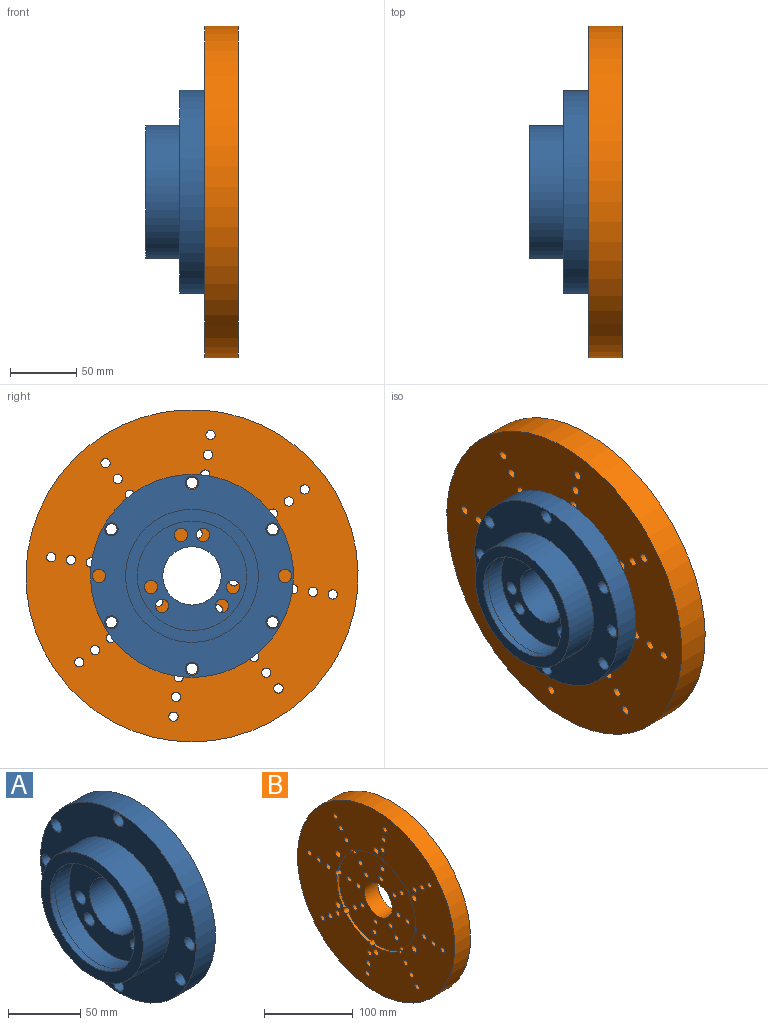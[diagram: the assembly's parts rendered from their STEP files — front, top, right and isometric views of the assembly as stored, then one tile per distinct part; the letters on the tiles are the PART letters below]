
ASSEMBLY  parts=2 mates=1
PART A: 59 faces, bbox 47.5x152.8x152.8 mm
  f0: cylinder r=8mm len=16mm, axis (1,0,0), area 508.6mm2, adj f7,f19,f31,f32
  f1: cylinder r=8mm len=16mm, axis (1,0,0), area 508.6mm2, adj f7,f19,f31,f32
  f2: cylinder r=8mm len=16mm, axis (1,0,0), area 508.6mm2, adj f7,f22,f29,f30
  f3: cylinder r=8mm len=15.96mm, axis (1,0,0), area 508.6mm2, adj f7,f22,f29,f30
  f4: cylinder r=8mm len=15.96mm, axis (1,0,0), area 508.6mm2, adj f7,f25,f27,f28
  f5: cylinder r=8mm len=16mm, axis (1,0,0), area 508.6mm2, adj f7,f25,f27,f28
  f6: cylinder r=22mm len=44mm, axis (-1,0,0), area 3870.4mm2, adj f7,f17
  f7: plane 125x125mm, normal (1,0,0), area 9095.5mm2, adj f0,f1,f2,f3,f4,f5,f6,f8
  f8: cylinder r=62.5mm len=125mm, axis (-1,0,0), area 1178.1mm2, adj f7,f9
  f9: plane 152.75x152.75mm, normal (1,0,0), area 5425.2mm2, adj f8,f10,f33,f34,f35,f36,f37,f38
  f10: cylinder r=76.38mm len=152.75mm, axis (-1,0,0), area 9069.7mm2, adj f9,f11
  f11: plane 152.75x152.75mm, normal (-1,0,0), area 9843.1mm2, adj f10,f12,f33,f34,f35,f36,f37,f38
  f12: cylinder r=50mm len=100mm, axis (-1,0,0), area 8042.5mm2, adj f11,f13
  f13: plane 100x100mm, normal (-1,0,0), area 2508.4mm2, adj f12,f14
  f14: cylinder r=41.25mm len=82.5mm, axis (-1,0,0), area 1295.9mm2, adj f13,f15
  f15: plane 84x84mm, normal (1,0,0), area 196.2mm2, adj f14,f16
  f16: cylinder r=42mm len=84mm, axis (-1,0,0), area 3826.5mm2, adj f15,f17
  f17: plane 84x84mm, normal (-1,0,0), area 3550mm2, adj f6,f16,f18,f20,f21,f23,f24,f26
  f18: cylinder r=5mm len=13mm, axis (1,0,0), area 408.4mm2, adj f17,f19
  f19: plane 32.54x17.09mm, normal (1,0,0), area 298.2mm2, adj f0,f1,f18,f20,f31,f32
  f20: cylinder r=5mm len=13mm, axis (1,0,0), area 408.4mm2, adj f17,f19
  f21: cylinder r=5mm len=13mm, axis (1,0,0), area 408.4mm2, adj f17,f22
  f22: plane 30.32x24.27mm, normal (1,0,0), area 298.2mm2, adj f2,f3,f21,f23,f29,f30
  f23: cylinder r=5mm len=13mm, axis (1,0,0), area 408.4mm2, adj f17,f22
  f24: cylinder r=5mm len=13mm, axis (1,0,0), area 408.4mm2, adj f17,f25
  f25: plane 30.32x24.27mm, normal (1,0,0), area 298.2mm2, adj f4,f5,f24,f26,f27,f28
  f26: cylinder r=5mm len=13mm, axis (1,0,0), area 408.4mm2, adj f17,f25
  f27: cylinder r=8mm len=15mm, axis (1,0,0), area 163mm2, adj f4,f5,f7,f25
  f28: cylinder r=8mm len=15mm, axis (1,0,0), area 100.2mm2, adj f4,f5,f7,f25
  f29: cylinder r=8mm len=15mm, axis (1,0,0), area 163mm2, adj f2,f3,f7,f22
  f30: cylinder r=8mm len=15mm, axis (1,0,0), area 100.2mm2, adj f2,f3,f7,f22
  f31: cylinder r=8mm len=15mm, axis (1,0,0), area 163mm2, adj f0,f1,f7,f19
  f32: cylinder r=8mm len=15mm, axis (1,0,0), area 100.2mm2, adj f0,f1,f7,f19
  f33: cylinder r=5mm len=18.9mm, axis (1,0,0), area 593.8mm2, adj f9,f11
  f34: cylinder r=5mm len=18.9mm, axis (1,0,0), area 593.8mm2, adj f9,f11
  f35: cylinder r=5mm len=18.9mm, axis (1,0,0), area 593.8mm2, adj f9,f11
  f36: cylinder r=5mm len=18.9mm, axis (1,0,0), area 593.8mm2, adj f9,f11
  f37: cylinder r=5mm len=18.9mm, axis (1,0,0), area 593.8mm2, adj f9,f11
  f38: cylinder r=5mm len=18.9mm, axis (1,0,0), area 593.8mm2, adj f9,f11
  f39: cylinder r=5mm len=18.9mm, axis (1,0,0), area 593.8mm2, adj f9,f11
  f40: cylinder r=5mm len=18.9mm, axis (1,0,0), area 593.8mm2, adj f9,f11
  f41: cylinder r=2.5mm len=23mm, axis (1,0,0), area 361.3mm2, adj f7,f42
  f42: cone r=0mm half-angle=59deg, axis (1,0,0), area 22.9mm2, adj f41
  f43: cylinder r=2.5mm len=23mm, axis (1,0,0), area 361.3mm2, adj f7,f44
  f44: cone r=0mm half-angle=59deg, axis (1,0,0), area 22.9mm2, adj f43
  f45: cylinder r=2.5mm len=23mm, axis (1,0,0), area 361.3mm2, adj f7,f46
  f46: cone r=0mm half-angle=59deg, axis (1,0,0), area 22.9mm2, adj f45
  f47: cylinder r=3.5mm len=19mm, axis (1,0,0), area 417.8mm2, adj f7,f48
  f48: cone r=0mm half-angle=59deg, axis (1,0,0), area 44.9mm2, adj f47
  f49: cylinder r=3.5mm len=19mm, axis (1,0,0), area 417.8mm2, adj f7,f50
  f50: cone r=0mm half-angle=59deg, axis (1,0,0), area 44.9mm2, adj f49
  f51: cylinder r=3.5mm len=19mm, axis (1,0,0), area 417.8mm2, adj f7,f52
  f52: cone r=0mm half-angle=59deg, axis (1,0,0), area 44.9mm2, adj f51
  f53: cylinder r=3.5mm len=19mm, axis (1,0,0), area 417.8mm2, adj f7,f54
  f54: cone r=0mm half-angle=59deg, axis (1,0,0), area 44.9mm2, adj f53
  f55: cylinder r=3.5mm len=19mm, axis (1,0,0), area 417.8mm2, adj f7,f56
  f56: cone r=0mm half-angle=59deg, axis (1,0,0), area 44.9mm2, adj f55
  f57: cylinder r=3.5mm len=19mm, axis (1,0,0), area 417.8mm2, adj f7,f58
  f58: cone r=0mm half-angle=59deg, axis (1,0,0), area 44.9mm2, adj f57
PART B: 67 faces, bbox 25x250x250 mm
  f0: cylinder r=62.5mm len=39.95mm, axis (1,0,0), area 147.5mm2, adj f8,f12,f46,f54
  f1: cylinder r=62.5mm len=35.82mm, axis (1,0,0), area 147.5mm2, adj f8,f12,f38,f54
  f2: cylinder r=62.5mm len=35.82mm, axis (1,0,0), area 147.5mm2, adj f8,f12,f51,f52
  f3: cylinder r=62.5mm len=39.95mm, axis (1,0,0), area 147.5mm2, adj f8,f12,f27,f52
  f4: cylinder r=62.5mm len=39.95mm, axis (1,0,0), area 147.5mm2, adj f8,f12,f45,f51
  f5: cylinder r=62.5mm len=35.82mm, axis (1,0,0), area 147.5mm2, adj f8,f12,f27,f46
  f6: cylinder r=62.5mm len=35.82mm, axis (1,0,0), area 147.5mm2, adj f8,f12,f41,f45
  f7: cylinder r=62.5mm len=39.95mm, axis (1,0,0), area 147.5mm2, adj f8,f12,f38,f41
  f8: plane 125x125mm, normal (-1,0,0), area 9950mm2, adj f0,f1,f2,f3,f4,f5,f6,f7
  f9: cylinder r=22mm len=44mm, axis (1,0,0), area 2971.9mm2, adj f8,f10
  f10: plane 250x250mm, normal (1,0,0), area 45379.1mm2, adj f9,f11,f13,f14,f15,f16,f17,f18
  f11: cylinder r=125mm len=250mm, axis (1,0,0), area 19635mm2, adj f10,f12
  f12: plane 250x250mm, normal (-1,0,0), area 35429.2mm2, adj f0,f1,f2,f3,f4,f5,f6,f7
  f13: cylinder r=4.25mm len=25mm, axis (-1,0,0), area 667.6mm2, adj f10,f12
  f14: cylinder r=4.25mm len=25mm, axis (-1,0,0), area 667.6mm2, adj f10,f12
  f15: cylinder r=4.25mm len=25mm, axis (-1,0,0), area 667.6mm2, adj f10,f12
  f16: cylinder r=4.25mm len=25mm, axis (-1,0,0), area 667.6mm2, adj f10,f12
  f17: cylinder r=4.25mm len=25mm, axis (-1,0,0), area 667.6mm2, adj f10,f12
  f18: cylinder r=4.25mm len=25mm, axis (-1,0,0), area 667.6mm2, adj f10,f12
  f19: cylinder r=3.5mm len=21.5mm, axis (-1,0,0), area 472.8mm2, adj f8,f10
  f20: cylinder r=3.5mm len=25mm, axis (-1,0,0), area 549.8mm2, adj f10,f12
  f21: cylinder r=3.5mm len=25mm, axis (-1,0,0), area 549.8mm2, adj f10,f12
  f22: cylinder r=3.5mm len=25mm, axis (-1,0,0), area 549.8mm2, adj f10,f12
  f23: cylinder r=3.5mm len=25mm, axis (-1,0,0), area 549.8mm2, adj f10,f12
  f24: cylinder r=3.5mm len=25mm, axis (-1,0,0), area 549.8mm2, adj f10,f12
  f25: cylinder r=3.5mm len=25mm, axis (-1,0,0), area 549.8mm2, adj f10,f12
  f26: cylinder r=3.5mm len=25mm, axis (-1,0,0), area 549.8mm2, adj f10,f12
  f27: cylinder r=3.5mm len=25mm, axis (-1,0,0), area 507.8mm2, adj f3,f5,f8,f10,f12
  f28: cylinder r=3.5mm len=21.5mm, axis (-1,0,0), area 472.8mm2, adj f8,f10
  f29: cylinder r=3.5mm len=21.5mm, axis (-1,0,0), area 472.8mm2, adj f8,f10
  f30: cylinder r=3.5mm len=25mm, axis (-1,0,0), area 549.8mm2, adj f10,f12
  f31: cylinder r=3.5mm len=21.5mm, axis (-1,0,0), area 472.8mm2, adj f8,f10
  f32: cylinder r=3.5mm len=21.5mm, axis (-1,0,0), area 472.8mm2, adj f8,f10
  f33: cylinder r=3.5mm len=21.5mm, axis (-1,0,0), area 472.8mm2, adj f8,f10
  f34: cylinder r=3.5mm len=25mm, axis (-1,0,0), area 549.8mm2, adj f10,f12
  f35: cylinder r=3.5mm len=25mm, axis (-1,0,0), area 549.8mm2, adj f10,f12
  f36: cylinder r=3.5mm len=25mm, axis (-1,0,0), area 549.8mm2, adj f10,f12
  f37: cylinder r=3.5mm len=21.5mm, axis (-1,0,0), area 472.8mm2, adj f8,f10
  f38: cylinder r=3.5mm len=25mm, axis (-1,0,0), area 507.8mm2, adj f1,f7,f8,f10,f12
  f39: cylinder r=3.5mm len=21.5mm, axis (-1,0,0), area 472.8mm2, adj f8,f10
  f40: cylinder r=3.5mm len=21.5mm, axis (-1,0,0), area 472.8mm2, adj f8,f10
  f41: cylinder r=3.5mm len=25mm, axis (-1,0,0), area 507.8mm2, adj f6,f7,f8,f10,f12
  f42: cylinder r=3.5mm len=21.5mm, axis (-1,0,0), area 472.8mm2, adj f8,f10
  f43: cylinder r=3.5mm len=25mm, axis (-1,0,0), area 549.8mm2, adj f10,f12
  f44: cylinder r=3.5mm len=25mm, axis (-1,0,0), area 549.8mm2, adj f10,f12
  f45: cylinder r=3.5mm len=25mm, axis (-1,0,0), area 507.8mm2, adj f4,f6,f8,f10,f12
  f46: cylinder r=3.5mm len=25mm, axis (-1,0,0), area 507.8mm2, adj f0,f5,f8,f10,f12
  f47: cylinder r=3.5mm len=25mm, axis (-1,0,0), area 549.8mm2, adj f10,f12
  f48: cylinder r=3.5mm len=25mm, axis (-1,0,0), area 549.8mm2, adj f10,f12
  f49: cylinder r=3.5mm len=21.5mm, axis (-1,0,0), area 472.8mm2, adj f8,f10
  f50: cylinder r=3.5mm len=25mm, axis (-1,0,0), area 549.8mm2, adj f10,f12
  f51: cylinder r=3.5mm len=25mm, axis (-1,0,0), area 507.8mm2, adj f2,f4,f8,f10,f12
  f52: cylinder r=3.5mm len=25mm, axis (-1,0,0), area 507.8mm2, adj f2,f3,f8,f10,f12
  f53: cylinder r=3.5mm len=25mm, axis (-1,0,0), area 549.8mm2, adj f10,f12
  f54: cylinder r=3.5mm len=25mm, axis (-1,0,0), area 507.8mm2, adj f0,f1,f8,f10,f12
  f55: cylinder r=3.5mm len=25mm, axis (-1,0,0), area 549.8mm2, adj f10,f12
  f56: cylinder r=3.5mm len=25mm, axis (-1,0,0), area 549.8mm2, adj f10,f12
  f57: cylinder r=3.5mm len=25mm, axis (-1,0,0), area 549.8mm2, adj f10,f12
  f58: cylinder r=3.5mm len=25mm, axis (-1,0,0), area 549.8mm2, adj f10,f12
  f59: cylinder r=3.5mm len=21.5mm, axis (-1,0,0), area 472.8mm2, adj f8,f10
  f60: cylinder r=3.5mm len=21.5mm, axis (-1,0,0), area 472.8mm2, adj f8,f10
  f61: cylinder r=3.5mm len=21.5mm, axis (-1,0,0), area 472.8mm2, adj f8,f10
  f62: cylinder r=3.5mm len=21.5mm, axis (-1,0,0), area 472.8mm2, adj f8,f10
  f63: cylinder r=3.5mm len=21.5mm, axis (-1,0,0), area 472.8mm2, adj f8,f10
  f64: cylinder r=3.5mm len=25mm, axis (-1,0,0), area 549.8mm2, adj f10,f12
  f65: cylinder r=3.5mm len=25mm, axis (-1,0,0), area 549.8mm2, adj f10,f12
  f66: cylinder r=3.5mm len=25mm, axis (-1,0,0), area 549.8mm2, adj f10,f12
PLACE A at identity fixed
PLACE B t=(44.5,0,0)mm
MATE revolute A.f6 <-> B.f0  axis (1,0,0) through (44.5,0,0)mm
